# Revit family: NLRS_63_LF_UN_noodverlichting HXN300_htk
name_source: partatom
category: Lighting Fixtures
units: mm (PartAtom-declared; Revit-internal decimal feet)

## family parameters
Always vertical = Yes
Cut with Voids When Loaded = No
Light Source = Yes
OmniClass Number = 23.85.30.21
OmniClass Title = Environmental Detection/Registration
Part Type = Normal
Room Calculation Point = No
Round Connector Dimension = Use Radius
Shared = No
Work Plane-Based = No

## types (2) — shared parameters
Apparent Load = 0 VA
Color Filter = 16777215
Dimming Lamp Color Temperature Shift = <None>
Emit from Line Length = 610 mm
Manufacturer = Hertek
NLRS_C_breedte = 90 mm  [stored 0.295276 ft]
NLRS_C_code_fabrikant_gln = 8714253082646
NLRS_C_hoogte = 170 mm  [stored 0.557743 ft]
NLRS_C_lengte = 340 mm  [stored 1.11549 ft]
NLRS_C_materiaal = Polycarbonaat wit
NLRS_C_materiaal_01 = Glass
NLRS_C_materiaal_kleur = wit
NLRS_C_revit_versie = 2019
NLRS_E_c01_radius = 8 mm  [stored 0.0262467 ft]
NLRS_E_c01_schijnbaar_vermogen = 0 VA
NLRS_E_c01_schijnbaar_vermogen_fase_1 = 0 VA
NLRS_E_c01_schijnbaar_vermogen_fase_2 = 0 VA
NLRS_E_c01_schijnbaar_vermogen_fase_3 = 0 VA
NLRS_E_spanning = 230 V
NLRS_E_stroom = 0.0 A
NLRS_S_gewicht_netto = 0.00 kg
Photometric Web File = none
Tilt Angle = 90.00°
URL = www.hertek.eu
buispendelset 0.5m = NLRS_63_LF_UN_buispendelset_htk : universele pendelbuisset 0.5m_htk_HRA011
buispendelset 1m = NLRS_63_LF_UN_buispendelset_htk : universele pendelbuisset 1.0m_htk_HRA021
centraal = No
decentraal = Yes
draadpendelset 1.5m = NLRS_63_LF_UN_draadpendelset_htk : universele draadpendelset 1.5m_htk_HRA040
vermogensclassificatie = NV

## per-type parameters (varying)
| type | IP65 kit | NLRS_C_code_artikel | NLRS_C_model | NLRS_C_omschrijving | NLRS_E_IPwaarde | picto | wireless | zichtbaar_01 |
| regular wireless 230v_htk_HXW321 | Yes | HXW321 | HXN300 dec WL opbouw | HXN300 dec WL opbouw wand picto | 65 | Yes | Yes | Yes |
| HXN300 dec AT opbouw plafond nood_htk_HXD351 | No | HXD351 | HXN300 dec AT opbouw plafond nood | HXN300 dec AT opbouw plafond nood | 42 | No | No | No |

note: [stored X ft] marks values corroborated as IEEE doubles in the binary element streams (Revit-internal decimal feet)

## geometry (parser evidence)
native form markers: Blend x12, Sweep x50
no freeform markers — native parametric forms only
